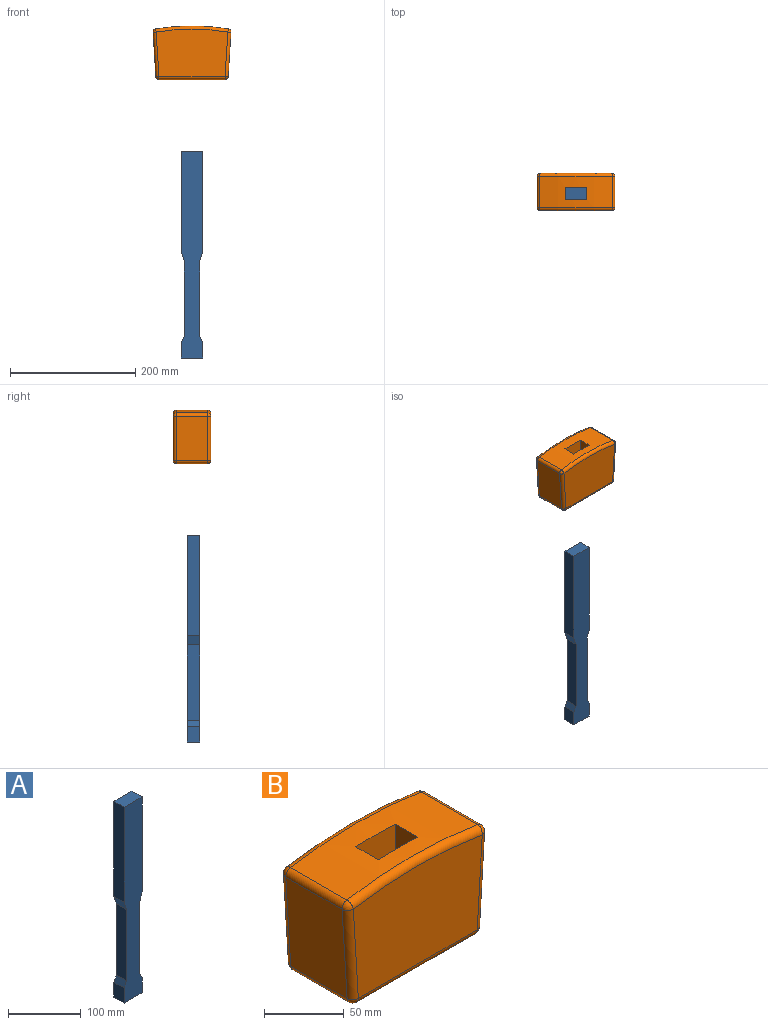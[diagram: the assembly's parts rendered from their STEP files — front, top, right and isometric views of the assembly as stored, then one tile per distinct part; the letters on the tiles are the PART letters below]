
ASSEMBLY  parts=2 mates=1
PART A: 14 faces, bbox 35x20x330 mm
  f0: plane 35x20mm, normal (0,0,1), area 700mm2, adj f1,f11,f12,f13
  f1: plane 160x20mm, normal (-1,0,0), area 3200mm2, adj f0,f2,f12,f13
  f2: plane 20x15mm, normal (-0.95,0,-0.32), area 316.2mm2, adj f1,f3,f12,f13
  f3: plane 120x20mm, normal (-1,0,0), area 2400mm2, adj f2,f4,f12,f13
  f4: plane 20x10mm, normal (-0.89,0,0.45), area 223.6mm2, adj f3,f5,f12,f13
  f5: plane 25x20mm, normal (-1,0,0), area 500mm2, adj f4,f6,f12,f13
  f6: plane 35x20mm, normal (0,0,-1), area 700mm2, adj f5,f7,f12,f13
  f7: plane 25x20mm, normal (1,0,0), area 500mm2, adj f6,f8,f12,f13
  f8: plane 20x10mm, normal (0.89,0,0.45), area 223.6mm2, adj f7,f9,f12,f13
  f9: plane 120x20mm, normal (1,0,0), area 2400mm2, adj f8,f10,f12,f13
  f10: plane 20x15mm, normal (0.95,0,-0.32), area 316.2mm2, adj f9,f11,f12,f13
  f11: plane 160x20mm, normal (1,0,0), area 3200mm2, adj f0,f10,f12,f13
  f12: plane 330x35mm, normal (0,-1,0), area 10225mm2, adj f0,f1,f2,f3,f4,f5,f6,f7
  f13: plane 330x35mm, normal (0,1,0), area 10225mm2, adj f0,f1,f2,f3,f4,f5,f6,f7
PART B: 30 faces, bbox 124.5x60x90.4 mm
  f0: cylinder r=354.76mm len=116.1mm, axis (0,1,0), area 5130.7mm2, adj f14,f19,f22,f25,f26,f27,f28,f29
  f1: plane 105.61x50mm, normal (0,0,-1), area 4580.3mm2, adj f6,f10,f11,f12,f26,f27,f28,f29
  f2: plane 70.84x50mm, normal (-1,0,-0.06), area 3548.7mm2, adj f11,f20,f21,f25
  f3: plane 70.84x50mm, normal (1,0,-0.06), area 3548.7mm2, adj f6,f9,f13,f14
  f4: plane 114.46x75.55mm, normal (0,-1,0), area 8154.4mm2, adj f9,f10,f19,f20
  f5: plane 114.46x75.55mm, normal (0,1,0), area 8154.4mm2, adj f12,f13,f21,f22
  f6: cylinder r=5mm len=50mm, axis (0,-1,0), area 377.1mm2, adj f1,f3,f7,f8
  f7: sphere r=5mm, area 37.7mm2, adj f6,f9,f10
  f8: sphere r=5mm, area 37.7mm2, adj f6,f12,f13
  f9: cylinder r=5mm len=71.15mm, axis (-0.06,0,-1), area 557.4mm2, adj f3,f4,f7,f15
  f10: cylinder r=5mm len=105.61mm, axis (-1,0,0), area 829.4mm2, adj f1,f4,f7,f16
  f11: cylinder r=5mm len=50mm, axis (0,1,0), area 377.1mm2, adj f1,f2,f16,f17
  f12: cylinder r=5mm len=105.61mm, axis (1,0,0), area 829.4mm2, adj f1,f5,f8,f17
  f13: cylinder r=5mm len=71.15mm, axis (0.06,0,1), area 557.4mm2, adj f3,f5,f8,f18
  f14: cylinder r=5mm len=50mm, axis (0,1,0), area 367.2mm2, adj f0,f3,f15,f18
  f15: sphere r=5mm, area 36.7mm2, adj f9,f14,f19
  f16: sphere r=5mm, area 37.7mm2, adj f10,f11,f20
  f17: sphere r=5mm, area 37.7mm2, adj f11,f12,f21
  f18: sphere r=5mm, area 36.7mm2, adj f13,f14,f22
  f19: torus R=349.76mm, axis (0,-1,0), area 911.2mm2, adj f0,f4,f15,f23
  f20: cylinder r=5mm len=71.15mm, axis (-0.06,0,1), area 557.4mm2, adj f2,f4,f16,f23
  f21: cylinder r=5mm len=71.15mm, axis (0.06,0,-1), area 557.4mm2, adj f2,f5,f17,f24
  f22: torus R=349.76mm, axis (0,-1,0), area 911.2mm2, adj f0,f5,f18,f24
  f23: sphere r=5mm, area 36.7mm2, adj f19,f20,f25
  f24: sphere r=5mm, area 36.7mm2, adj f21,f22,f25
  f25: cylinder r=5mm len=50mm, axis (0,1,0), area 367.2mm2, adj f0,f2,f23,f24
  f26: plane 85.55x35mm, normal (0,1,0), area 2989.2mm2, adj f0,f1,f28,f29
  f27: plane 85.55x35mm, normal (0,-1,0), area 2989.2mm2, adj f0,f1,f28,f29
  f28: plane 85.12x20mm, normal (1,0,0), area 1702.3mm2, adj f0,f1,f26,f27
  f29: plane 85.12x20mm, normal (-1,0,0), area 1702.3mm2, adj f0,f1,f26,f27
PLACE A t=(19.7,-22.5,-212.69)mm
PLACE B t=(0,0,85)mm
MATE fastened A.f12 <-> B.f26  axis (0,-1,0) through (37.2,-42.5,-48.32)mm
